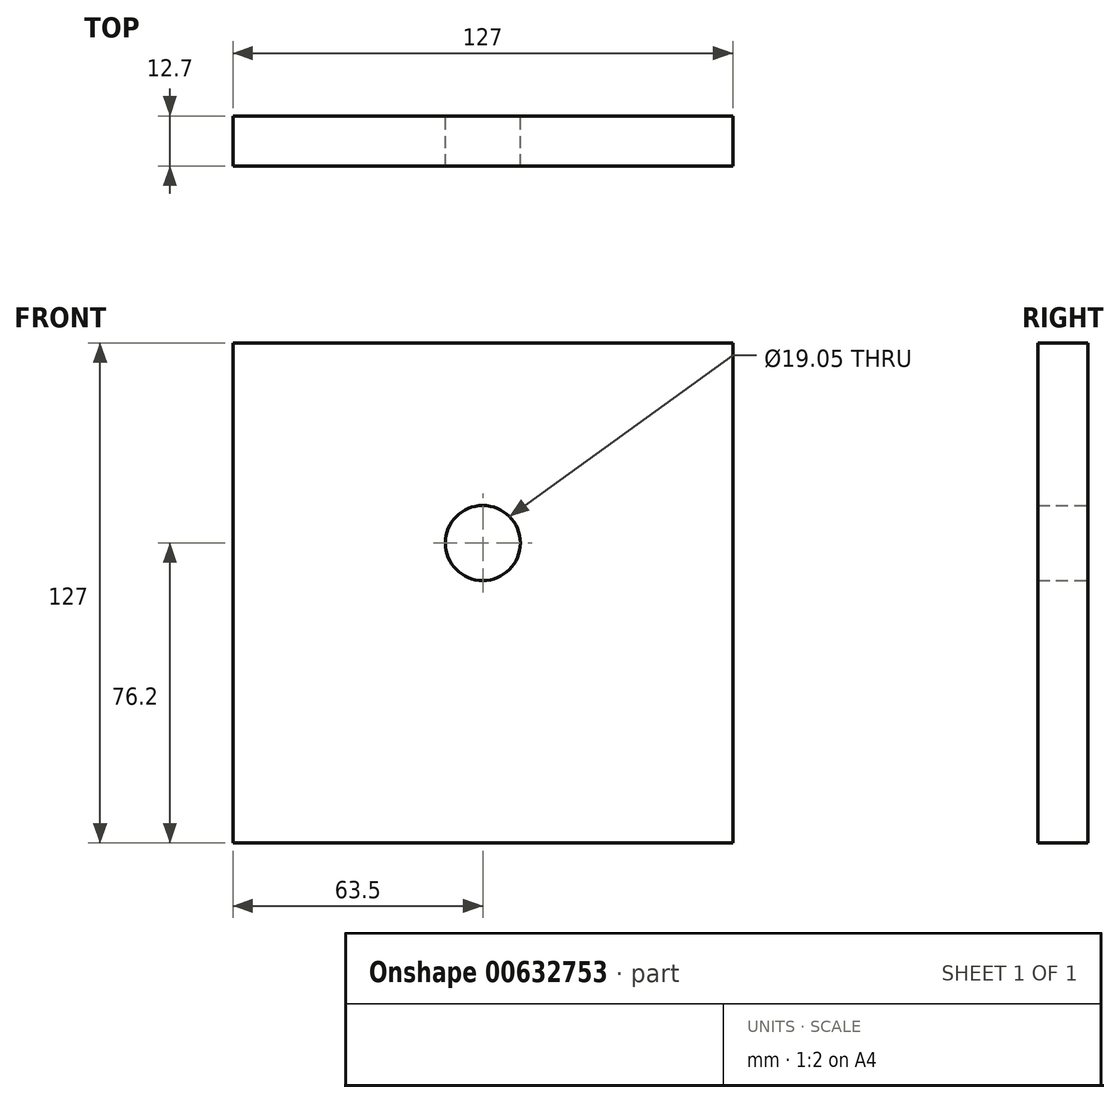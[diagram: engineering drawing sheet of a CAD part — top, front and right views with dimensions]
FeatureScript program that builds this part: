
annotation { "Feature Type Name" : "Feature", "Feature Type Description" : "" }
export const myFeature = defineFeature(function(context is Context, id is Id, definition is map)
    precondition{}
    {
        {
            var Q0;
            Q0=qCreatedBy(makeId("Front.planeOp"),FACE);
            var sketch = newSketch(context, id + "F0", { "sketchPlane" : qUnion([Q0])});
            skLineSegment(sketch, "E0.bottom", {"start": v(-63.5, 63.5) * mm, "end": v(63.5, 63.5) * mm});
            skLineSegment(sketch, "E0.top", {"start": v(-63.5, -63.5) * mm, "end": v(63.5, -63.5) * mm});
            skLineSegment(sketch, "E0.left", {"start": v(-63.5, 63.5) * mm, "end": v(-63.5, -63.5) * mm});
            skLineSegment(sketch, "E0.right", {"start": v(63.5, 63.5) * mm, "end": v(63.5, -63.5) * mm});
            skPoint(sketch, "E0.middle", {"position": v(0, 0) * mm});
            skPoint(sketch, "E1", {"position": v(0, 12.7) * mm});
            skCircle(sketch, "E2", {"center": v(0, 12.7) * mm, "radius": 9.53 * mm});
            skSolve(sketch);
        }
        {
            var Q0;
            Q0=makeQuery(id+"F0.imprint","IMPRINT",FACE,{"disambiguationData":[TD([[makeQuery(id+"F0.imprint","IMPRINT",EDGE,{"derivedFrom":sQuery(id+"F0.wireOp",EDGE,"E0.bottom")}),-1.0]])]});
            extrude(context, id + "F1", {"entities" : qUnion([Q0]), "endBound" : BoundingType.SYMMETRIC, "depth" : 12.7 * mm, "offsetDistance" : 25.4 * mm});
        }
    });
